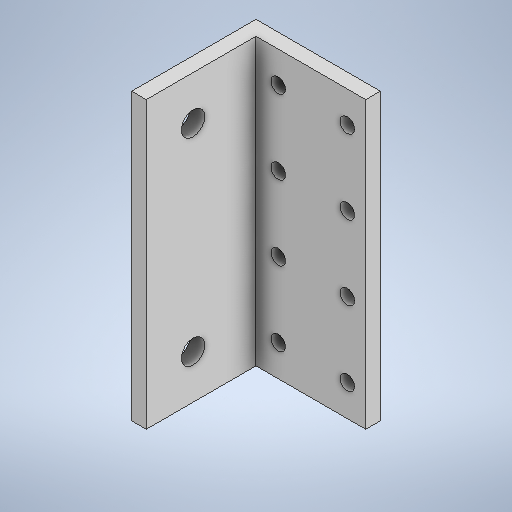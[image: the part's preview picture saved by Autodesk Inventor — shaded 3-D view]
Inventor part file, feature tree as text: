
AUTODESK INVENTOR PART (.ipt)
format: ipt  version: 2025.1 (Build 291241000, 241)  size: 303,616 bytes
history: native  units: in
note: dims shown in document units (in); Inventor stores cm internally (conversion verified against a paired STEP export)
features: extrude x6, sketch x6, direct_edit x3, move_body x3
ambient origin geometry x8: Origin, YZ Plane, XZ Plane, XY Plane, X Axis, Y Axis, Z Axis, Center Point
bodies: Solid1 (feature_tree)
feature tree (18):
  extrude  "Extrusion1"  Depth=1.063in
  extrude  "Extrusion2"  Depth=0.125in
  direct_edit  "Direct Edit1"
  extrude  "Extrusion3"  Depth=0.535in TaperAngle=0.0deg
  direct_edit  "Direct Edit2"
  extrude  "Extrusion4"  Depth=0.315in
  direct_edit  "Direct Edit3"
  extrude  "Extrusion5"  Depth=0.125in
  extrude  "Extrusion6"  Depth=0.125in
  sketch  "Sketch1"  dims[d0=1.063in d1=1.063in]
  sketch  "Sketch2"  dims[d2=0.125in d3=0.125in]
  sketch  "Sketch4"  dims[d4=90.0deg d5=0.535in d6=0.0in]
  sketch  "Sketch5"  dims[d7=0.535in d8=0.315in]
  sketch  "Sketch6"  dims[d9=0.125in d10=0.59in]
  sketch  "Sketch7"  dims[d11=180.0deg d12=0.125in d13=0.635in d14=0.0in d15=0.0in d16=0.0in d17=0.635in d18=0.535in d19=0.315in d20=180.0deg d21=0.125in d22=0.59in d23=0.125in d24=0.535in d25=0.0in d26=0.0in d27=0.0in d28=0.635in d29=0.535in d31=0.315in d32=0.125in d33=0.59in d34=0.125in d35=0.535in d36=0.0in d37=0.0in d38=0.0in d39=0.635in d40=0.535in d41=0.315in d42=0.125in d43=0.59in d44=180.0deg d45=0.125in d46=0.535in d47=0.0in d48=0.4in d49=0.375in d50=90.0deg d51=0.4in d52=0.375in d53=270.0deg d54=0.2in d55=0.2in d56=0.535in d57=0.0in]
  move_body  "Move1"
  move_body  "Move2"
  move_body  "Move3"
